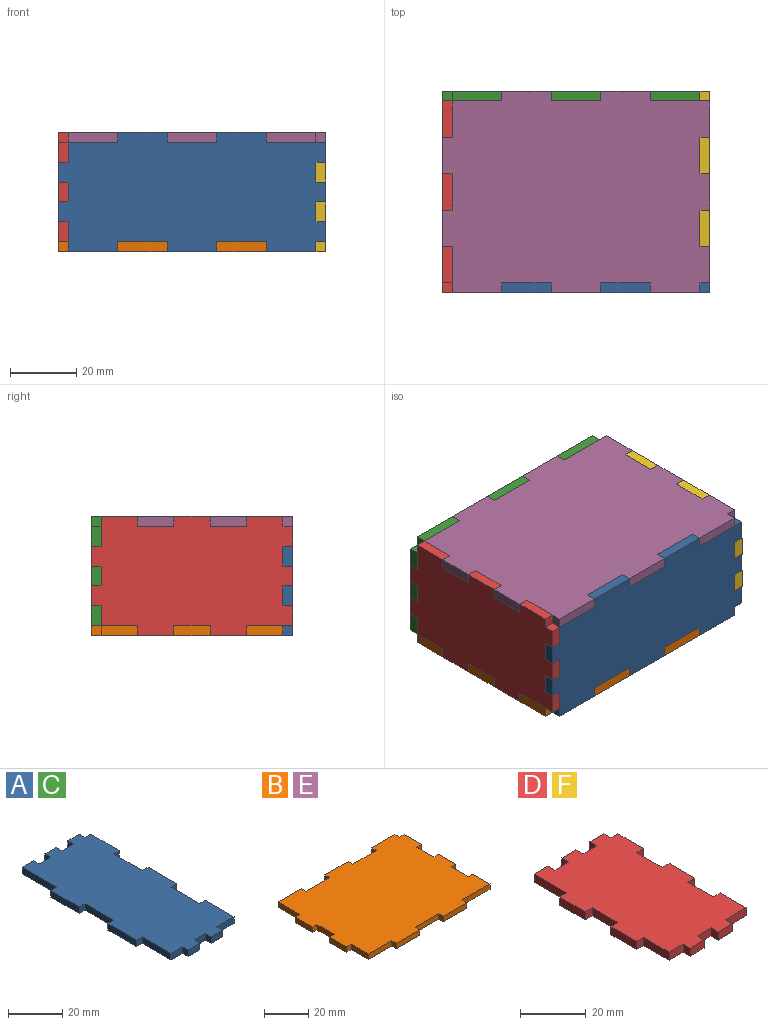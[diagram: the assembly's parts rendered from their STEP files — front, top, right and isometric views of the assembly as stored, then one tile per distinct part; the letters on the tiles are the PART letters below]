
ASSEMBLY  parts=6 mates=4
PART A: 40 faces, bbox 36x81x3 mm
  f0: plane 3x3mm, normal (-1,0,0), area 9mm2, adj f1,f37,f38,f39
  f1: plane 6x3mm, normal (0,1,0), area 18mm2, adj f0,f2,f38,f39
  f2: plane 3x3mm, normal (1,0,0), area 9mm2, adj f1,f3,f38,f39
  f3: plane 6x3mm, normal (0,1,0), area 18mm2, adj f2,f4,f38,f39
  f4: plane 3x3mm, normal (-1,0,0), area 9mm2, adj f3,f5,f38,f39
  f5: plane 6x3mm, normal (0,1,0), area 18mm2, adj f4,f6,f38,f39
  f6: plane 3x3mm, normal (1,0,0), area 9mm2, adj f5,f7,f38,f39
  f7: plane 6x3mm, normal (0,1,0), area 18mm2, adj f6,f8,f38,f39
  f8: plane 18x3mm, normal (-1,0,0), area 54mm2, adj f7,f9,f38,f39
  f9: plane 3x3mm, normal (0,1,0), area 9mm2, adj f8,f10,f38,f39
  f10: plane 15x3mm, normal (-1,0,0), area 45mm2, adj f9,f11,f38,f39
  f11: plane 3x3mm, normal (0,-1,0), area 9mm2, adj f10,f12,f38,f39
  f12: plane 15x3mm, normal (-1,0,0), area 45mm2, adj f11,f13,f38,f39
  f13: plane 3x3mm, normal (0,1,0), area 9mm2, adj f12,f14,f38,f39
  f14: plane 15x3mm, normal (-1,0,0), area 45mm2, adj f13,f15,f38,f39
  f15: plane 3x3mm, normal (0,-1,0), area 9mm2, adj f14,f16,f38,f39
  f16: plane 15x3mm, normal (-1,0,0), area 45mm2, adj f15,f17,f38,f39
  f17: plane 6x3mm, normal (0,-1,0), area 18mm2, adj f16,f18,f38,f39
  f18: plane 3x3mm, normal (-1,0,0), area 9mm2, adj f17,f19,f38,f39
  f19: plane 6x3mm, normal (0,-1,0), area 18mm2, adj f18,f20,f38,f39
  f20: plane 3x3mm, normal (1,0,0), area 9mm2, adj f19,f21,f38,f39
  f21: plane 6x3mm, normal (0,-1,0), area 18mm2, adj f20,f22,f38,f39
  f22: plane 3x3mm, normal (-1,0,0), area 9mm2, adj f21,f23,f38,f39
  f23: plane 6x3mm, normal (0,-1,0), area 18mm2, adj f22,f24,f38,f39
  f24: plane 3x3mm, normal (1,0,0), area 9mm2, adj f23,f25,f38,f39
  f25: plane 9x3mm, normal (0,-1,0), area 27mm2, adj f24,f26,f38,f39
  f26: plane 15x3mm, normal (1,0,0), area 45mm2, adj f25,f27,f38,f39
  f27: plane 3x3mm, normal (0,1,0), area 9mm2, adj f26,f28,f38,f39
  f28: plane 15x3mm, normal (1,0,0), area 45mm2, adj f27,f29,f38,f39
  f29: plane 3x3mm, normal (0,-1,0), area 9mm2, adj f28,f30,f38,f39
  f30: plane 15x3mm, normal (1,0,0), area 45mm2, adj f29,f31,f38,f39
  f31: plane 3x3mm, normal (0,1,0), area 9mm2, adj f30,f32,f38,f39
  f32: plane 15x3mm, normal (1,0,0), area 45mm2, adj f31,f33,f38,f39
  f33: plane 3x3mm, normal (0,-1,0), area 9mm2, adj f32,f34,f38,f39
  f34: plane 15x3mm, normal (1,0,0), area 45mm2, adj f33,f35,f38,f39
  f35: plane 3x3mm, normal (0,1,0), area 9mm2, adj f34,f36,f38,f39
  f36: plane 3x3mm, normal (1,0,0), area 9mm2, adj f35,f37,f38,f39
  f37: plane 6x3mm, normal (0,1,0), area 18mm2, adj f0,f36,f38,f39
  f38: plane 81x36mm, normal (0,0,1), area 2565mm2, adj f0,f1,f2,f3,f4,f5,f6,f7
  f39: plane 81x36mm, normal (0,0,-1), area 2565mm2, adj f0,f1,f2,f3,f4,f5,f6,f7
PART B: 40 faces, bbox 81x61x3 mm
  f0: plane 14x3mm, normal (-1,0,0), area 42mm2, adj f1,f37,f38,f39
  f1: plane 3x3mm, normal (0,1,0), area 9mm2, adj f0,f2,f38,f39
  f2: plane 11x3mm, normal (-1,0,0), area 33mm2, adj f1,f3,f38,f39
  f3: plane 3x3mm, normal (0,-1,0), area 9mm2, adj f2,f4,f38,f39
  f4: plane 11x3mm, normal (-1,0,0), area 33mm2, adj f3,f5,f38,f39
  f5: plane 3x3mm, normal (0,1,0), area 9mm2, adj f4,f6,f38,f39
  f6: plane 11x3mm, normal (-1,0,0), area 33mm2, adj f5,f7,f38,f39
  f7: plane 3x3mm, normal (0,-1,0), area 9mm2, adj f6,f8,f38,f39
  f8: plane 11x3mm, normal (-1,0,0), area 33mm2, adj f7,f9,f38,f39
  f9: plane 15x3mm, normal (0,-1,0), area 45mm2, adj f8,f10,f38,f39
  f10: plane 3x3mm, normal (-1,0,0), area 9mm2, adj f9,f11,f38,f39
  f11: plane 15x3mm, normal (0,-1,0), area 45mm2, adj f10,f12,f38,f39
  f12: plane 3x3mm, normal (1,0,0), area 9mm2, adj f11,f13,f38,f39
  f13: plane 15x3mm, normal (0,-1,0), area 45mm2, adj f12,f14,f38,f39
  f14: plane 3x3mm, normal (-1,0,0), area 9mm2, adj f13,f15,f38,f39
  f15: plane 15x3mm, normal (0,-1,0), area 45mm2, adj f14,f16,f38,f39
  f16: plane 3x3mm, normal (1,0,0), area 9mm2, adj f15,f17,f38,f39
  f17: plane 18x3mm, normal (0,-1,0), area 54mm2, adj f16,f18,f38,f39
  f18: plane 11x3mm, normal (1,0,0), area 33mm2, adj f17,f19,f38,f39
  f19: plane 3x3mm, normal (0,1,0), area 9mm2, adj f18,f20,f38,f39
  f20: plane 11x3mm, normal (1,0,0), area 33mm2, adj f19,f21,f38,f39
  f21: plane 3x3mm, normal (0,-1,0), area 9mm2, adj f20,f22,f38,f39
  f22: plane 11x3mm, normal (1,0,0), area 33mm2, adj f21,f23,f38,f39
  f23: plane 3x3mm, normal (0,1,0), area 9mm2, adj f22,f24,f38,f39
  f24: plane 11x3mm, normal (1,0,0), area 33mm2, adj f23,f25,f38,f39
  f25: plane 3x3mm, normal (0,-1,0), area 9mm2, adj f24,f26,f38,f39
  f26: plane 11x3mm, normal (1,0,0), area 33mm2, adj f25,f27,f38,f39
  f27: plane 3x3mm, normal (0,1,0), area 9mm2, adj f26,f28,f38,f39
  f28: plane 3x3mm, normal (1,0,0), area 9mm2, adj f27,f29,f38,f39
  f29: plane 15x3mm, normal (0,1,0), area 45mm2, adj f28,f30,f38,f39
  f30: plane 3x3mm, normal (-1,0,0), area 9mm2, adj f29,f31,f38,f39
  f31: plane 15x3mm, normal (0,1,0), area 45mm2, adj f30,f32,f38,f39
  f32: plane 3x3mm, normal (1,0,0), area 9mm2, adj f31,f33,f38,f39
  f33: plane 15x3mm, normal (0,1,0), area 45mm2, adj f32,f34,f38,f39
  f34: plane 3x3mm, normal (-1,0,0), area 9mm2, adj f33,f35,f38,f39
  f35: plane 15x3mm, normal (0,1,0), area 45mm2, adj f34,f36,f38,f39
  f36: plane 3x3mm, normal (1,0,0), area 9mm2, adj f35,f37,f38,f39
  f37: plane 15x3mm, normal (0,1,0), area 45mm2, adj f0,f36,f38,f39
  f38: plane 81x61mm, normal (0,0,1), area 4515mm2, adj f0,f1,f2,f3,f4,f5,f6,f7
  f39: plane 81x61mm, normal (0,0,-1), area 4515mm2, adj f0,f1,f2,f3,f4,f5,f6,f7
PART C: same geometry as A
PART D: 40 faces, bbox 36x61x3 mm
  f0: plane 6x3mm, normal (0,1,0), area 18mm2, adj f1,f37,f38,f39
  f1: plane 3x3mm, normal (-1,0,0), area 9mm2, adj f0,f2,f38,f39
  f2: plane 6x3mm, normal (0,1,0), area 18mm2, adj f1,f3,f38,f39
  f3: plane 3x3mm, normal (1,0,0), area 9mm2, adj f2,f4,f38,f39
  f4: plane 6x3mm, normal (0,1,0), area 18mm2, adj f3,f5,f38,f39
  f5: plane 3x3mm, normal (-1,0,0), area 9mm2, adj f4,f6,f38,f39
  f6: plane 6x3mm, normal (0,1,0), area 18mm2, adj f5,f7,f38,f39
  f7: plane 3x3mm, normal (1,0,0), area 9mm2, adj f6,f8,f38,f39
  f8: plane 6x3mm, normal (0,1,0), area 18mm2, adj f7,f9,f38,f39
  f9: plane 14x3mm, normal (-1,0,0), area 42mm2, adj f8,f10,f38,f39
  f10: plane 3x3mm, normal (0,1,0), area 9mm2, adj f9,f11,f38,f39
  f11: plane 11x3mm, normal (-1,0,0), area 33mm2, adj f10,f12,f38,f39
  f12: plane 3x3mm, normal (0,-1,0), area 9mm2, adj f11,f13,f38,f39
  f13: plane 11x3mm, normal (-1,0,0), area 33mm2, adj f12,f14,f38,f39
  f14: plane 3x3mm, normal (0,1,0), area 9mm2, adj f13,f15,f38,f39
  f15: plane 11x3mm, normal (-1,0,0), area 33mm2, adj f14,f16,f38,f39
  f16: plane 3x3mm, normal (0,-1,0), area 9mm2, adj f15,f17,f38,f39
  f17: plane 11x3mm, normal (-1,0,0), area 33mm2, adj f16,f18,f38,f39
  f18: plane 6x3mm, normal (0,-1,0), area 18mm2, adj f17,f19,f38,f39
  f19: plane 3x3mm, normal (-1,0,0), area 9mm2, adj f18,f20,f38,f39
  f20: plane 6x3mm, normal (0,-1,0), area 18mm2, adj f19,f21,f38,f39
  f21: plane 3x3mm, normal (1,0,0), area 9mm2, adj f20,f22,f38,f39
  f22: plane 6x3mm, normal (0,-1,0), area 18mm2, adj f21,f23,f38,f39
  f23: plane 3x3mm, normal (-1,0,0), area 9mm2, adj f22,f24,f38,f39
  f24: plane 6x3mm, normal (0,-1,0), area 18mm2, adj f23,f25,f38,f39
  f25: plane 3x3mm, normal (1,0,0), area 9mm2, adj f24,f26,f38,f39
  f26: plane 9x3mm, normal (0,-1,0), area 27mm2, adj f25,f27,f38,f39
  f27: plane 11x3mm, normal (1,0,0), area 33mm2, adj f26,f28,f38,f39
  f28: plane 3x3mm, normal (0,1,0), area 9mm2, adj f27,f29,f38,f39
  f29: plane 11x3mm, normal (1,0,0), area 33mm2, adj f28,f30,f38,f39
  f30: plane 3x3mm, normal (0,-1,0), area 9mm2, adj f29,f31,f38,f39
  f31: plane 11x3mm, normal (1,0,0), area 33mm2, adj f30,f32,f38,f39
  f32: plane 3x3mm, normal (0,1,0), area 9mm2, adj f31,f33,f38,f39
  f33: plane 11x3mm, normal (1,0,0), area 33mm2, adj f32,f34,f38,f39
  f34: plane 3x3mm, normal (0,-1,0), area 9mm2, adj f33,f35,f38,f39
  f35: plane 11x3mm, normal (1,0,0), area 33mm2, adj f34,f36,f38,f39
  f36: plane 3x3mm, normal (0,1,0), area 9mm2, adj f35,f37,f38,f39
  f37: plane 3x3mm, normal (1,0,0), area 9mm2, adj f0,f36,f38,f39
  f38: plane 61x36mm, normal (0,0,1), area 1905mm2, adj f0,f1,f2,f3,f4,f5,f6,f7
  f39: plane 61x36mm, normal (0,0,-1), area 1905mm2, adj f0,f1,f2,f3,f4,f5,f6,f7
PART E: same geometry as B
PART F: same geometry as D
PLACE A rot(axis=(0.58,0.58,-0.58),120deg) t=(-92.68,-205.16,-316.32)mm
PLACE B rot(axis=(0,-1,0),180deg) t=(-92.68,-177.66,-197.86)mm
PLACE C rot(axis=(0.58,-0.58,0.58),120deg) t=(-92.68,-147.16,-49.4)mm
PLACE D rot(axis=(0.71,0,0.71),180deg) t=(-133.18,-177.66,40.92)mm
PLACE E rot(axis=(1,0,0),180deg) t=(-92.68,-177.66,-164.86)mm
PLACE F rot(axis=(0,1,0),90deg) t=(-55.18,-177.66,-406.63)mm
MATE fastened F.f16 <-> E.f25  axis (0,-1,0) through (-53.68,-194.16,-166.36)mm
MATE fastened B.f7 <-> F.f28  axis (0,-1,0) through (-53.68,-194.16,-199.36)mm
MATE fastened A.f24 <-> D.f7  axis (0,0,-1) through (-131.68,-206.66,-191.86)mm
MATE fastened C.f18 <-> F.f1  axis (0,0,-1) through (-53.68,-148.66,-191.86)mm
